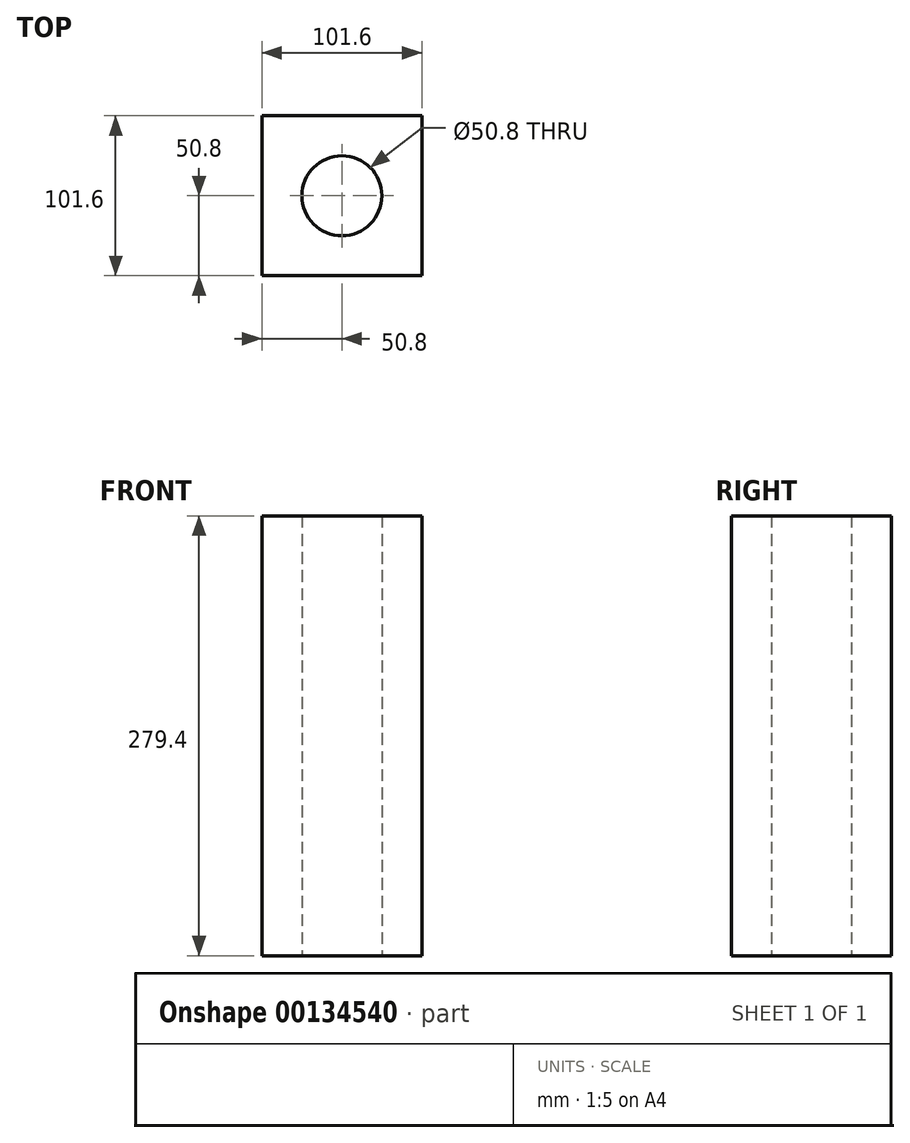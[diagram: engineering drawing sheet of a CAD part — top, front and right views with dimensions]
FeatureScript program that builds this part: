
annotation { "Feature Type Name" : "Feature", "Feature Type Description" : "" }
export const myFeature = defineFeature(function(context is Context, id is Id, definition is map)
    precondition{}
    {
        {
            var Q0;
            Q0=qCreatedBy(makeId("Top.planeOp"),FACE);
            var sketch = newSketch(context, id + "F0", { "sketchPlane" : qUnion([Q0])});
            skLineSegment(sketch, "E0", {"start": v(0, 0) * mm, "end": v(50.8, 0) * mm});
            skLineSegment(sketch, "E1", {"start": v(0, 0) * mm, "end": v(-50.8, 0) * mm});
            skLineSegment(sketch, "E2", {"start": v(-50.8, 0) * mm, "end": v(-50.8, 50.8) * mm});
            skLineSegment(sketch, "E3", {"start": v(-50.8, 50.8) * mm, "end": v(50.8, 50.8) * mm});
            skLineSegment(sketch, "E4", {"start": v(50.8, 50.8) * mm, "end": v(50.8, -50.8) * mm});
            skLineSegment(sketch, "E5", {"start": v(50.8, -50.8) * mm, "end": v(-50.8, -50.8) * mm});
            skLineSegment(sketch, "E6", {"start": v(-50.8, -50.8) * mm, "end": v(-50.8, 0) * mm});
            skCircle(sketch, "E7", {"center": v(0, 0) * mm, "radius": 25.4 * mm});
            skSolve(sketch);
        }
        {
            var Q0;
            {var subQ1=sQuery(id+"F0.wireOp",EDGE,"E2");Q0=makeQuery(id+"F0.imprint","IMPRINT",FACE,{"disambiguationData":[TD([[makeQuery(id+"F0.imprint","IMPRINT",EDGE,{"derivedFrom":subQ1}),-1.0]])]});}
            var Q1;
            {var subQ0=sQuery(id+"F0.wireOp",EDGE,"E5");Q1=makeQuery(id+"F0.imprint","IMPRINT",FACE,{"disambiguationData":[TD([[makeQuery(id+"F0.imprint","IMPRINT",EDGE,{"derivedFrom":subQ0}),-1.0]])]});}
            extrude(context, id + "F1", {"entities" : qUnion([Q0, Q1]), "depth" : 279.4 * mm});
        }
    });
